# Revit family: LZ_SERIES
name_source: partatom
category: Lighting Fixtures
units: mm (PartAtom-declared; Revit-internal decimal feet)

## family parameters
Cut with Voids When Loaded = No
Host = Face
Light Source = Yes
OmniClass Number = 23.80.70.11.21
OmniClass Title = Emergency Lighting
Part Type = Normal
Room Calculation Point = No
Round Connector Dimension = Use Diameter
Shared = No

## types (2) — shared parameters
Color Filter = 16777215
Default Elevation = 48.000"
Description = Low-profile, easy to install emergency lighting unit
Dimming Lamp Color Temperature Shift = <None>
Family = Outdoor Emergency Lighting
Lamp = 2 HALOGEN LAMPS
Light Source Symbol Size = 0.400"
Manufacturer = Dual-Lite
Model = LZ
Reflector = Glass
URL = https://www.currentlighting.com
Wattage Comments = 5-10 W

## per-type parameters (varying)
| type | Backbox |
| LZ-Black | Black |
| LZ-White | White |

## geometry (parser evidence)
native form markers: Blend x3, Sweep x4
no freeform markers — native parametric forms only
